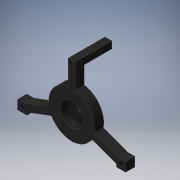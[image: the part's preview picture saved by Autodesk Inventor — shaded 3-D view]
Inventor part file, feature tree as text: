
AUTODESK INVENTOR PART (.ipt)
format: ipt  version: 2016 (Build 200138000, 138)  size: 207,872 bytes
history: native  units: mm
features: extrude x5, sketch x3, other x1, projected_geometry x1
ambient origin geometry x8: Origin, YZ Plane, XZ Plane, XY Plane, X Axis, Y Axis, Z Axis, Center Point
bodies: Body1 (feature_tree)
feature tree (10):
  other  "ソリッド1"
  extrude  "押し出し1"  Depth=32.0mm
  extrude  "押し出し3"  Depth=2.0mm
  sketch  "スケッチ6"
  extrude  "押し出し7"  Depth=27.0mm
  extrude  "押し出し9"  Depth=30.0mm
  extrude  "押し出し10"  Depth=3.0mm
  sketch  "スケッチ8"
  sketch  "スケッチ7"
  projected_geometry  "投影ループ1"
